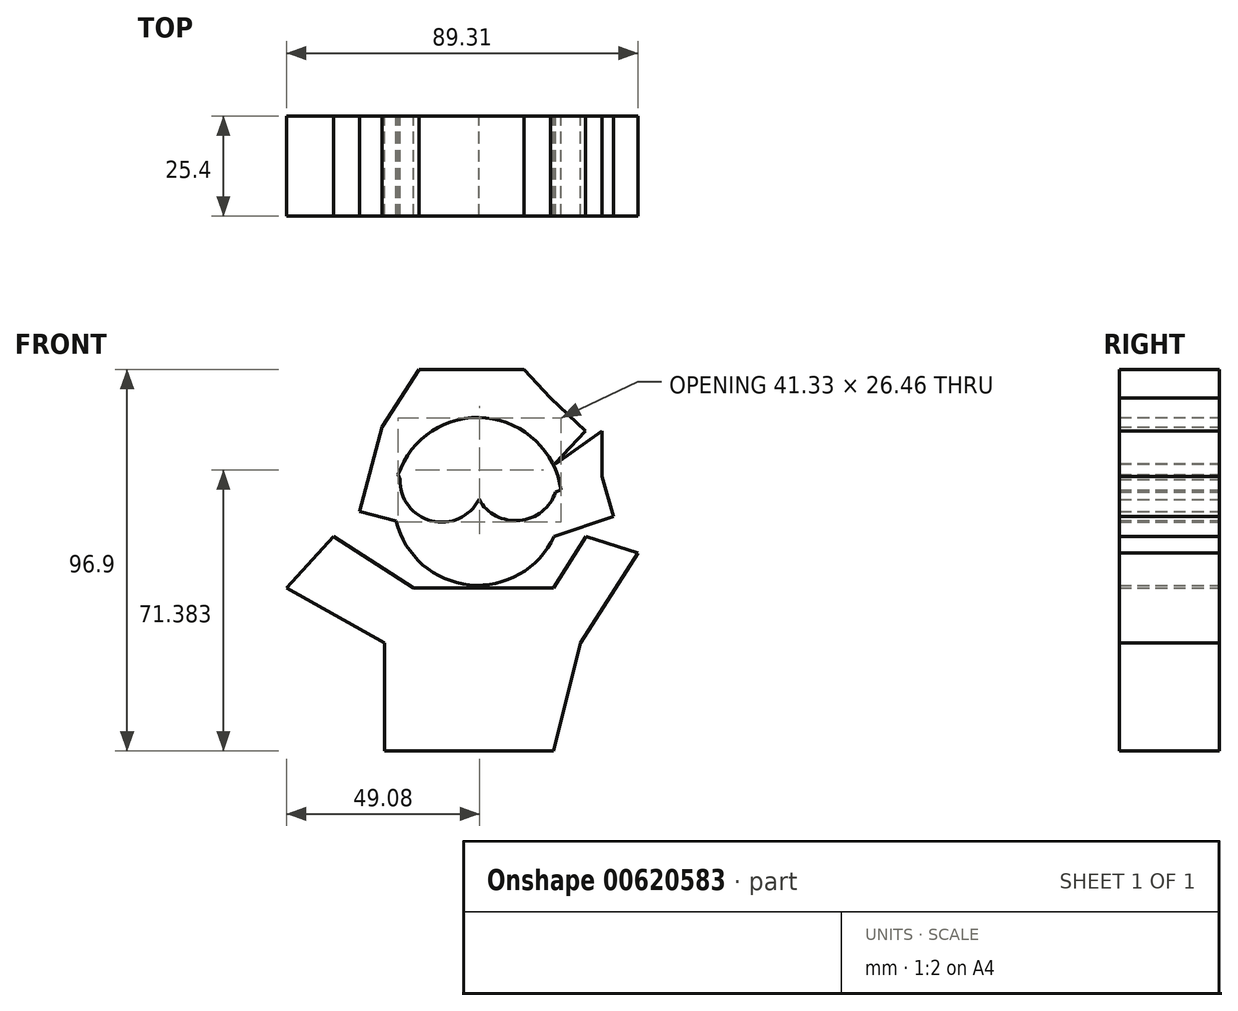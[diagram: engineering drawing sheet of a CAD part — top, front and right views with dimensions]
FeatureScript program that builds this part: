
annotation { "Feature Type Name" : "Feature", "Feature Type Description" : "" }
export const myFeature = defineFeature(function(context is Context, id is Id, definition is map)
    precondition{}
    {
        {
            var Q0;
            Q0=qCreatedBy(makeId("Front.planeOp"),FACE);
            var sketch = newSketch(context, id + "F0", { "sketchPlane" : qUnion([Q0])});
            skLineSegment(sketch, "E0", {"start": v(0, 0) * mm, "end": v(-23.62, -35.66) * mm});
            skLineSegment(sketch, "E1", {"start": v(-23.62, -35.66) * mm, "end": v(-40.7, -19.81) * mm});
            skLineSegment(sketch, "E2", {"start": v(-40.7, -19.81) * mm, "end": v(-23.62, -1.43) * mm});
            skLineSegment(sketch, "E3", {"start": v(0, 0) * mm, "end": v(-23.62, 0) * mm});
            skLineSegment(sketch, "E4", {"start": v(0, 0) * mm, "end": v(14.17, -35.66) * mm});
            skLineSegment(sketch, "E5", {"start": v(14.17, -35.66) * mm, "end": v(33.38, -23.16) * mm});
            skLineSegment(sketch, "E6", {"start": v(33.38, -23.16) * mm, "end": v(19.23, -1.43) * mm});
            skLineSegment(sketch, "E7", {"start": v(0, 0) * mm, "end": v(19.23, 0) * mm});
            skLineSegment(sketch, "E8", {"start": v(-23.62, 0) * mm, "end": v(-23.62, 27.43) * mm});
            skLineSegment(sketch, "E9", {"start": v(-23.62, 27.43) * mm, "end": v(-48.62, 41.45) * mm});
            skLineSegment(sketch, "E10", {"start": v(-48.62, 41.45) * mm, "end": v(-36.58, 54.42) * mm});
            skLineSegment(sketch, "E11", {"start": v(-36.58, 54.42) * mm, "end": v(-16.3, 41.45) * mm});
            skLineSegment(sketch, "E12", {"start": v(-16.3, 41.45) * mm, "end": v(19.23, 41.45) * mm});
            skLineSegment(sketch, "E13", {"start": v(19.23, 41.45) * mm, "end": v(27.52, 54.42) * mm});
            skLineSegment(sketch, "E14", {"start": v(27.52, 54.42) * mm, "end": v(40.7, 50.3) * mm});
            skLineSegment(sketch, "E15", {"start": v(40.7, 50.3) * mm, "end": v(26.07, 27.43) * mm});
            skLineSegment(sketch, "E16", {"start": v(26.07, 27.43) * mm, "end": v(19.23, 0) * mm});
            skCircle(sketch, "E17", {"center": v(0, 63.4) * mm, "radius": 21.31 * mm});
            skLineSegment(sketch, "E18", {"start": v(0, 84.71) * mm, "end": v(0, 96.9) * mm});
            skLineSegment(sketch, "E19", {"start": v(0, 96.9) * mm, "end": v(11.7, 96.9) * mm});
            skLineSegment(sketch, "E20", {"start": v(11.7, 96.9) * mm, "end": v(18.48, 89.6) * mm});
            skLineSegment(sketch, "E21", {"start": v(18.48, 89.6) * mm, "end": v(14.82, 80.2) * mm});
            skLineSegment(sketch, "E22", {"start": v(14.82, 80.2) * mm, "end": v(18.48, 89.6) * mm});
            skLineSegment(sketch, "E23", {"start": v(18.48, 89.6) * mm, "end": v(27.35, 81.25) * mm});
            skLineSegment(sketch, "E24", {"start": v(27.35, 81.25) * mm, "end": v(19.22, 72.61) * mm});
            skLineSegment(sketch, "E25", {"start": v(19.22, 72.61) * mm, "end": v(31.52, 81.25) * mm});
            skLineSegment(sketch, "E26", {"start": v(31.52, 81.25) * mm, "end": v(31.52, 69.77) * mm});
            skLineSegment(sketch, "E27", {"start": v(31.52, 69.77) * mm, "end": v(19.22, 65.6) * mm});
            skLineSegment(sketch, "E28", {"start": v(19.22, 65.6) * mm, "end": v(31.52, 69.77) * mm});
            skLineSegment(sketch, "E29", {"start": v(31.52, 69.77) * mm, "end": v(34.54, 60.88) * mm});
            skLineSegment(sketch, "E30", {"start": v(38.3, 60.88) * mm, "end": v(19.22, 54.42) * mm});
            skLineSegment(sketch, "E31", {"start": v(19.22, 54.42) * mm, "end": v(34.54, 59.6) * mm});
            skLineSegment(sketch, "E32", {"start": v(34.54, 59.6) * mm, "end": v(31.52, 69.77) * mm});
            skLineSegment(sketch, "E33", {"start": v(0, 96.9) * mm, "end": v(-14.92, 96.9) * mm});
            skLineSegment(sketch, "E34", {"start": v(-14.92, 96.9) * mm, "end": v(-9.95, 82.25) * mm});
            skLineSegment(sketch, "E35", {"start": v(-9.95, 82.25) * mm, "end": v(-13.82, 80.2) * mm});
            skLineSegment(sketch, "E36", {"start": v(-13.82, 80.2) * mm, "end": v(-14.92, 96.9) * mm});
            skLineSegment(sketch, "E37", {"start": v(-14.92, 96.9) * mm, "end": v(-24.3, 82.25) * mm});
            skLineSegment(sketch, "E38", {"start": v(-24.3, 82.25) * mm, "end": v(-18.64, 65.6) * mm});
            skLineSegment(sketch, "E39", {"start": v(-18.64, 65.6) * mm, "end": v(-24.3, 82.25) * mm});
            skLineSegment(sketch, "E40", {"start": v(-24.3, 82.25) * mm, "end": v(-30.05, 60.88) * mm});
            skLineSegment(sketch, "E41", {"start": v(-30.05, 60.88) * mm, "end": v(-20.7, 58.36) * mm});
            skLineSegment(sketch, "E42", {"start": v(-20.7, 58.36) * mm, "end": v(-19.75, 54.42) * mm});
            skLineSegment(sketch, "E43", {"start": v(-19.75, 54.42) * mm, "end": v(-30.05, 58.36) * mm});
            skCircle(sketch, "E44", {"center": v(-9.18, 68.72) * mm, "radius": 10.61 * mm});
            skCircle(sketch, "E45", {"center": v(9.6, 69.25) * mm, "radius": 10.76 * mm});
            skLineSegment(sketch, "E46", {"start": v(-5.53, 53.07) * mm, "end": v(9.6, 53.07) * mm});
            skLineSegment(sketch, "E47", {"start": v(9.6, 53.07) * mm, "end": v(-5.53, 53.07) * mm});
            skSolve(sketch);
        }
        {
            var Q0;
            Q0 = qSketchRegion(id + "F0", true);
            extrude(context, id + "F1", {"entities" : qUnion([Q0]), "depth" : 25.4 * mm, "offsetDistance" : 25.4 * mm});
        }
    });
